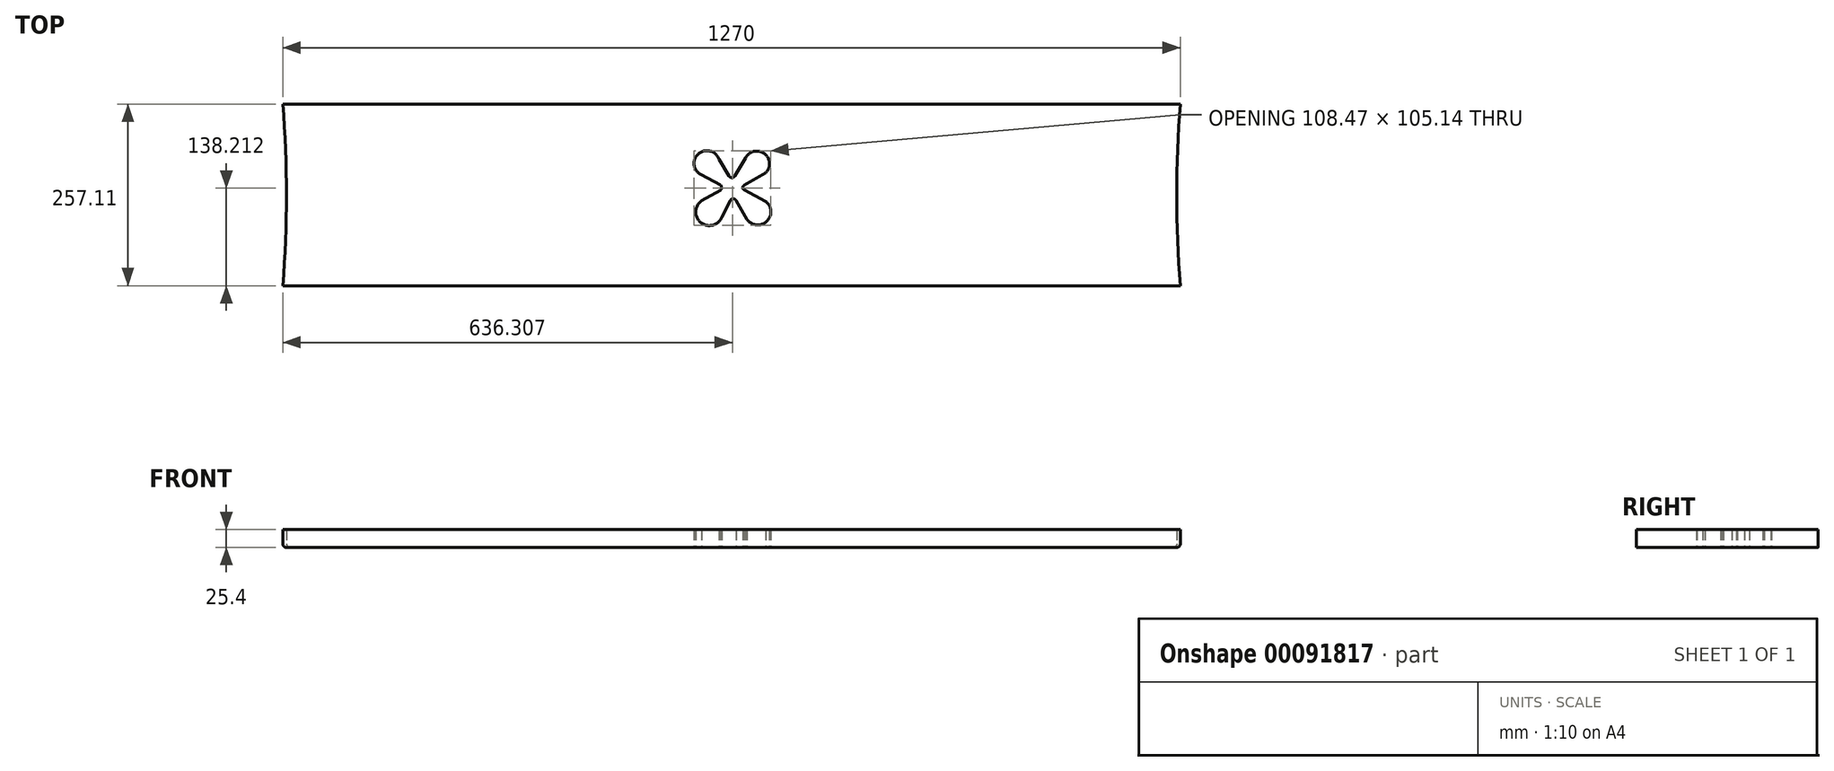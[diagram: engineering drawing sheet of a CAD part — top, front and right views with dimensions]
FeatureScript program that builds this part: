
annotation { "Feature Type Name" : "Feature", "Feature Type Description" : "" }
export const myFeature = defineFeature(function(context is Context, id is Id, definition is map)
    precondition{}
    {
        {
            var Q0;
            Q0=qCreatedBy(makeId("Top.planeOp"),FACE);
            var sketch = newSketch(context, id + "F0", { "sketchPlane" : qUnion([Q0])});
            skArc(sketch, "E0", {"start": v(-635, -139.73) * mm, "mid": v(-629.85, -11.18) * mm, "end": v(-635, 117.38) * mm});
            skArc(sketch, "E1", {"start": v(-17.83, 39.21) * mm, "mid": v(-46.75, 47.12) * mm, "end": v(-43.28, 17.34) * mm});
            skLineSegment(sketch, "E2", {"start": v(-43.28, 17.34) * mm, "end": v(-15.65, 3.03) * mm});
            skLineSegment(sketch, "E3", {"start": v(-17.83, 39.21) * mm, "end": v(-3.77, 15.68) * mm});
            skArc(sketch, "E4", {"start": v(-15.65, -4.42) * mm, "mid": v(-14.17, -0.7) * mm, "end": v(-15.65, 3.03) * mm});
            skArc(sketch, "E5", {"start": v(-3.77, 15.68) * mm, "mid": v(0.43, 13.3) * mm, "end": v(4.63, 15.68) * mm});
            skArc(sketch, "E6", {"start": v(-42.13, -19.4) * mm, "mid": v(-43.69, -50.2) * mm, "end": v(-13.77, -42.72) * mm});
            skLineSegment(sketch, "E7", {"start": v(-42.13, -19.4) * mm, "end": v(-15.65, -4.42) * mm});
            skLineSegment(sketch, "E8", {"start": v(-13.77, -42.72) * mm, "end": v(-1.85, -19.13) * mm});
            skArc(sketch, "E9", {"start": v(6.28, -19.13) * mm, "mid": v(2.22, -16.63) * mm, "end": v(-1.85, -19.13) * mm});
            skLineSegment(sketch, "E10", {"start": v(6.28, -19.13) * mm, "end": v(21.86, -45.86) * mm});
            skArc(sketch, "E11", {"start": v(21.86, -45.86) * mm, "mid": v(49.89, -48.46) * mm, "end": v(48.32, -20.35) * mm});
            skLineSegment(sketch, "E12", {"start": v(48.32, -20.35) * mm, "end": v(17.74, -4.26) * mm});
            skArc(sketch, "E13", {"start": v(17.15, 2.02) * mm, "mid": v(15.75, -1.28) * mm, "end": v(17.74, -4.26) * mm});
            skLineSegment(sketch, "E14", {"start": v(17.15, 2.02) * mm, "end": v(48.41, 20.24) * mm});
            skLineSegment(sketch, "E15", {"start": v(4.63, 15.68) * mm, "end": v(19.8, 41.04) * mm});
            skArc(sketch, "E16", {"start": v(48.41, 20.24) * mm, "mid": v(46.28, 47.4) * mm, "end": v(19.8, 41.04) * mm});
            skLineSegment(sketch, "E17", {"start": v(-635, 117.38) * mm, "end": v(0, 117.38) * mm});
            skLineSegment(sketch, "E18", {"start": v(-635, -139.73) * mm, "end": v(0, -139.73) * mm});
            skLineSegment(sketch, "E19.MirrorCS", {"start": v(635, 117.38) * mm, "end": v(0, 117.38) * mm});
            skArc(sketch, "E20.MirrorCS", {"start": v(635, -139.73) * mm, "mid": v(629.85, -11.18) * mm, "end": v(635, 117.38) * mm});
            skLineSegment(sketch, "E21.MirrorCS", {"start": v(635, -139.73) * mm, "end": v(0, -139.73) * mm});
            skLineSegment(sketch, "E22", {"start": v(-635, -139.73) * mm, "end": v(635, -139.73) * mm});
            skSolve(sketch);
        }
        {
            var Q0;
            {var subQ0=sQuery(id+"F0.wireOp",EDGE,"E0");Q0=makeQuery(id+"F0.imprint","IMPRINT",FACE,{"disambiguationData":[TD([[makeQuery(id+"F0.imprint","IMPRINT",EDGE,{"derivedFrom":subQ0}),-1.0]])]});}
            extrude(context, id + "F1", {"entities" : qUnion([Q0]), "depth" : 25.4 * mm});
        }
        {
            var Q0;
            Q0=makeQuery(id+"F1.opExtrude","CAP_EDGE",EDGE,{"disambiguationData":[OSD([sQuery(id+"F0.wireOp",EDGE,"E0")])],"isStart":true});
            fillet(context, id + "F2", {"entities" : qUnion([Q0]), "radius" : 5.08 * mm, "tangentPropagation" : true, "allowEdgeOverflow" : false});
        }
        {
            var Q0;
            Q0=makeQuery(id+"F1.opExtrude","CAP_EDGE",EDGE,{"disambiguationData":[OSD([sQuery(id+"F0.wireOp",EDGE,"E20.MirrorCS")])],"isStart":true});
            fillet(context, id + "F3", {"entities" : qUnion([Q0]), "radius" : 5.08 * mm, "tangentPropagation" : true, "allowEdgeOverflow" : false});
        }
    });
